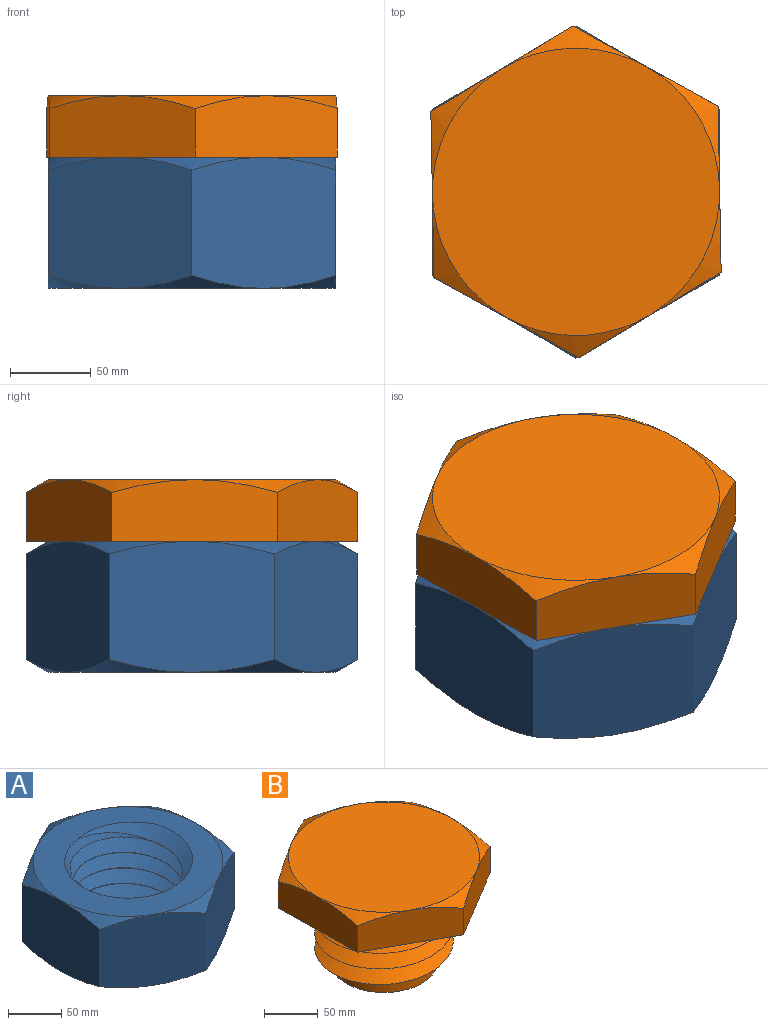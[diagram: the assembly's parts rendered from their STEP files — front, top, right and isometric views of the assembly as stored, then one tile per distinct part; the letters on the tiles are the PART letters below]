
ASSEMBLY  parts=2 mates=1
PART A: 24 faces, bbox 207.5x207.5x103.1 mm
  f0: cylinder r=50.8mm len=101.6mm, axis (0,0,-1), area -68mm2, adj f1,f21,f22,f23
  f1: plane 177.8x177.8mm, normal (0,0,-1), area 14134.9mm2, adj f0,f15,f16,f17,f18,f19,f20,f22
  f2: plane 88.9x81.31mm, normal (0.5,0.87,0), area 7784.5mm2, adj f3,f7,f9,f14,f15,f20
  f3: plane 88.9x81.31mm, normal (-0.5,0.87,0), area 7784.5mm2, adj f2,f4,f13,f14,f19,f20
  f4: plane 102.69x81.31mm, normal (-1,0,0), area 7784.5mm2, adj f3,f5,f12,f13,f18,f19
  f5: plane 88.9x81.31mm, normal (-0.5,-0.87,0), area 7784.5mm2, adj f4,f6,f11,f12,f17,f18
  f6: plane 88.9x81.31mm, normal (0.5,-0.87,0), area 7784.5mm2, adj f5,f7,f10,f11,f16,f17
  f7: plane 102.69x81.31mm, normal (1,0,0), area 7784.5mm2, adj f2,f6,f9,f10,f15,f16
  f8: plane 179.96x179.96mm, normal (0,0,1), area 13222mm2, adj f9,f10,f11,f12,f13,f14,f21,f22
  f9: cone r=159.29mm half-angle=60deg, axis (0,0,-1), area 490.5mm2, adj f2,f7,f8
  f10: cone r=159.29mm half-angle=60deg, axis (0,0,-1), area 490.5mm2, adj f6,f7,f8
  f11: cone r=159.29mm half-angle=60deg, axis (0,0,-1), area 490.5mm2, adj f5,f6,f8
  f12: cone r=159.29mm half-angle=60deg, axis (0,0,-1), area 490.5mm2, adj f4,f5,f8
  f13: cone r=159.29mm half-angle=60deg, axis (0,0,-1), area 490.5mm2, adj f3,f4,f8
  f14: cone r=159.29mm half-angle=60deg, axis (0,0,-1), area 490.5mm2, adj f2,f3,f8
  f15: cone r=159.29mm half-angle=60deg, axis (0,0,1), area 490.5mm2, adj f1,f2,f7
  f16: cone r=159.29mm half-angle=60deg, axis (0,0,1), area 490.5mm2, adj f1,f6,f7
  f17: cone r=159.29mm half-angle=60deg, axis (0,0,1), area 490.5mm2, adj f1,f5,f6
  f18: cone r=159.29mm half-angle=60deg, axis (0,0,1), area 490.5mm2, adj f1,f4,f5
  f19: cone r=159.29mm half-angle=60deg, axis (0,0,1), area 490.5mm2, adj f1,f3,f4
  f20: cone r=159.29mm half-angle=60deg, axis (0,0,1), area 490.5mm2, adj f1,f2,f3
  f21: cone r=50.8mm half-angle=45deg, axis (0,0,1), area 1293mm2, adj f0,f8,f22,f23
  f22: bspline ~138.52x131.74mm, area 28359.1mm2, adj f0,f1,f8,f21,f23
  f23: bspline ~138.52x131.74mm, area 28382.6mm2, adj f0,f1,f8,f21,f22
PART B: 19 faces, bbox 205.3x205.3x119.4 mm
  f0: plane 89.83x49.68mm, normal (0.48,0.88,0), area 3631.5mm2, adj f1,f5,f6,f8,f12
  f1: plane 87.94x52.96mm, normal (-0.52,0.86,0), area 3631.5mm2, adj f0,f2,f6,f11,f12
  f2: plane 102.64x38.11mm, normal (-1,-0.02,0), area 3631.5mm2, adj f1,f3,f6,f10,f11
  f3: plane 89.83x49.68mm, normal (-0.48,-0.88,0), area 3631.5mm2, adj f2,f4,f6,f9,f10
  f4: plane 87.94x52.96mm, normal (0.52,-0.86,0), area 3631.5mm2, adj f3,f5,f6,f7,f9
  f5: plane 102.64x38.11mm, normal (1,0.02,0), area 3631.5mm2, adj f0,f4,f6,f7,f8
  f6: plane 205.27x179.66mm, normal (0,0,-1), area 17169.7mm2, adj f0,f1,f2,f3,f4,f5,f14,f16
  f7: cone r=88.9mm half-angle=60deg, axis (0,0,-1), area 490.5mm2, adj f4,f5,f13
  f8: cone r=88.9mm half-angle=60deg, axis (0,0,-1), area 490.5mm2, adj f0,f5,f13
  f9: cone r=88.9mm half-angle=60deg, axis (0,0,-1), area 490.5mm2, adj f3,f4,f13
  f10: cone r=88.9mm half-angle=60deg, axis (0,0,-1), area 490.5mm2, adj f2,f3,f13
  f11: cone r=88.9mm half-angle=60deg, axis (0,0,-1), area 490.5mm2, adj f1,f2,f13
  f12: cone r=88.9mm half-angle=60deg, axis (0,0,-1), area 490.5mm2, adj f0,f1,f13
  f13: plane 177.8x177.8mm, normal (0,0,1), area 24828.7mm2, adj f7,f8,f9,f10,f11,f12
  f14: cylinder r=49.53mm len=99.06mm, axis (0,0,1), area 3492.8mm2, adj f6,f15,f16,f17,f18
  f15: plane 99.06x99.06mm, normal (0,0,-1), area 7707mm2, adj f14
  f16: bspline ~135.54x128.9mm, area 26667.6mm2, adj f6,f14,f17,f18
  f17: bspline ~135.54x128.9mm, area 23898.1mm2, adj f6,f14,f16,f18
  f18: plane 17.4x14.92mm, normal (0,-1,0), area 129.8mm2, adj f14,f16,f17
PLACE A rot(axis=(0.06,0.84,-0.54),0deg) t=(86.47,37.52,104.55)mm fixed
PLACE B t=(86.47,37.52,185.83)mm
MATE cylindrical B.f14 <-> A.f9  axis (0,0,-1) through (86.47,37.52,104.55)mm
